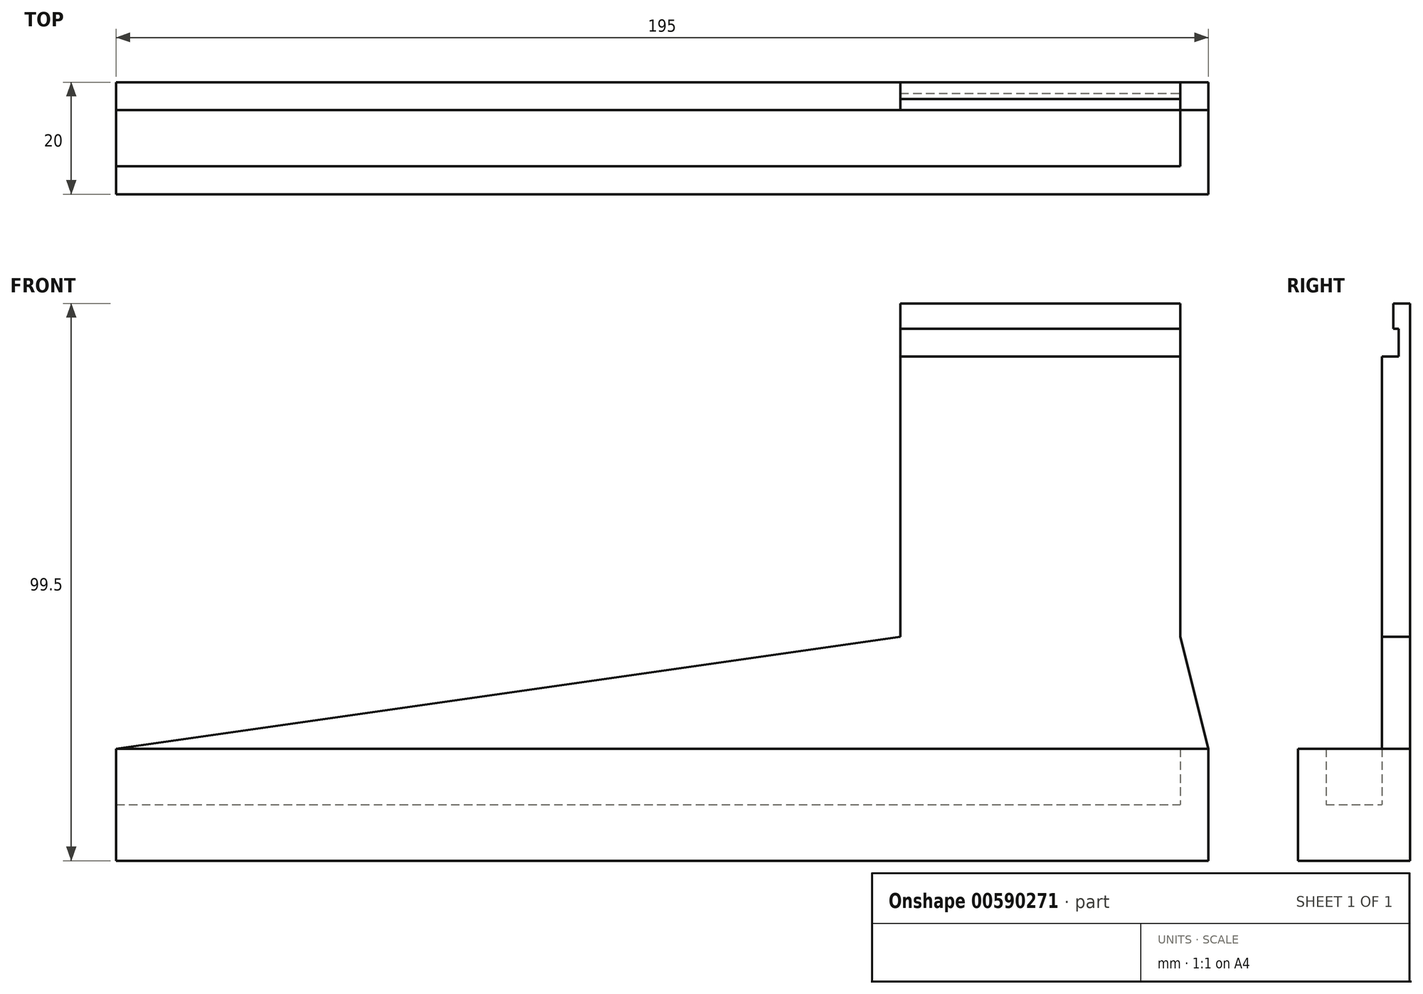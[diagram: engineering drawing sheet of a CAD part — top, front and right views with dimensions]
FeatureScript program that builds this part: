
annotation { "Feature Type Name" : "Feature", "Feature Type Description" : "" }
export const myFeature = defineFeature(function(context is Context, id is Id, definition is map)
    precondition{}
    {
        {
            var Q0;
            Q0=qCreatedBy(makeId("Top.planeOp"),FACE);
            var sketch = newSketch(context, id + "F0", { "sketchPlane" : qUnion([Q0])});
            skLineSegment(sketch, "E0.bottom", {"start": v(0, 0) * mm, "end": v(190, 0) * mm});
            skLineSegment(sketch, "E0.top", {"start": v(0, 5) * mm, "end": v(190, 5) * mm});
            skLineSegment(sketch, "E0.left", {"start": v(0, 0) * mm, "end": v(0, 5) * mm});
            skLineSegment(sketch, "E0.right", {"start": v(190, 0) * mm, "end": v(190, 5) * mm});
            skLineSegment(sketch, "E1.bottom", {"start": v(190, 0) * mm, "end": v(195, 0) * mm});
            skLineSegment(sketch, "E1.top", {"start": v(190, 20) * mm, "end": v(195, 20) * mm});
            skLineSegment(sketch, "E1.left", {"start": v(190, 0) * mm, "end": v(190, 20) * mm});
            skLineSegment(sketch, "E1.right", {"start": v(195, 0) * mm, "end": v(195, 20) * mm});
            skLineSegment(sketch, "E2.bottom", {"start": v(190, 20) * mm, "end": v(0, 20) * mm});
            skLineSegment(sketch, "E2.top", {"start": v(190, 15) * mm, "end": v(0, 15) * mm});
            skLineSegment(sketch, "E2.left", {"start": v(190, 20) * mm, "end": v(190, 15) * mm});
            skLineSegment(sketch, "E2.right", {"start": v(0, 20) * mm, "end": v(0, 15) * mm});
            skSolve(sketch);
        }
        {
            var Q0;
            Q0 = qSketchRegion(id + "F0", true);
            extrude(context, id + "F1", {"entities" : qUnion([Q0]), "depth" : 20 * mm, "offsetDistance" : 25 * mm});
        }
        {
            var Q0;
            Q0=qCreatedBy(makeId("Top.planeOp"),FACE);
            var sketch = newSketch(context, id + "F2", { "sketchPlane" : qUnion([Q0])});
            skLineSegment(sketch, "E3.bottom", {"start": v(0, 5) * mm, "end": v(190, 5) * mm});
            skLineSegment(sketch, "E3.top", {"start": v(0, 15) * mm, "end": v(190, 15) * mm});
            skLineSegment(sketch, "E3.left", {"start": v(0, 5) * mm, "end": v(0, 15) * mm});
            skLineSegment(sketch, "E3.right", {"start": v(190, 5) * mm, "end": v(190, 15) * mm});
            skSolve(sketch);
        }
        {
            var Q0;
            Q0 = qSketchRegion(id + "F2", true);
            extrude(context, id + "F3", {"entities" : qUnion([Q0]), "operationType" : NewBodyOperationType.ADD, "depth" : 10 * mm, "offsetDistance" : 25 * mm});
        }
        {
            var Q0;
            Q0=makeQuery(id+"F1.opExtrude","CAP_FACE",FACE,{"disambiguationData":[OSD([sQuery(id+"F0.wireOp",EDGE,"E0.bottom"),sQuery(id+"F0.wireOp",EDGE,"E0.top"),sQuery(id+"F0.wireOp",EDGE,"E0.left"),sQuery(id+"F0.wireOp",EDGE,"E1.bottom"),sQuery(id+"F0.wireOp",EDGE,"E1.top"),sQuery(id+"F0.wireOp",EDGE,"E1.left"),sQuery(id+"F0.wireOp",EDGE,"E1.right"),sQuery(id+"F0.wireOp",EDGE,"E2.bottom"),sQuery(id+"F0.wireOp",EDGE,"E2.top"),sQuery(id+"F0.wireOp",EDGE,"E2.right")])],"isStart":false});
            var sketch = newSketch(context, id + "F4", { "sketchPlane" : qUnion([Q0])});
            skLineSegment(sketch, "E4.bottom", {"start": v(190, 15) * mm, "end": v(140, 15) * mm});
            skLineSegment(sketch, "E4.top", {"start": v(190, 20) * mm, "end": v(140, 20) * mm});
            skLineSegment(sketch, "E4.left", {"start": v(190, 15) * mm, "end": v(190, 20) * mm});
            skLineSegment(sketch, "E4.right", {"start": v(140, 15) * mm, "end": v(140, 20) * mm});
            skSolve(sketch);
        }
        {
            var Q0;
            Q0 = qSketchRegion(id + "F4", true);
            extrude(context, id + "F5", {"entities" : qUnion([Q0]), "operationType" : NewBodyOperationType.ADD, "depth" : 70 * mm, "offsetDistance" : 25 * mm});
        }
        {
            var Q0;
            Q0=makeQuery(id+"F5.boolean.opBoolean","MERGE",FACE,{"derivedFrom":[makeQuery(id+"F1.opExtrude","SWEPT_FACE",FACE,{"disambiguationData":[OSD([sQuery(id+"F0.wireOp",EDGE,"E1.top"),sQuery(id+"F0.wireOp",EDGE,"E2.bottom")])]}),makeQuery(id+"F5.opExtrude","SWEPT_FACE",FACE,{"disambiguationData":[OSD([sQuery(id+"F4.wireOp",EDGE,"E4.top")])]})]});
            var sketch = newSketch(context, id + "F6", { "sketchPlane" : qUnion([Q0])});
            skLineSegment(sketch, "E5", {"start": v(-195, 20) * mm, "end": v(-190, 20) * mm});
            skLineSegment(sketch, "E6", {"start": v(-190, 20) * mm, "end": v(-190, 40) * mm});
            skLineSegment(sketch, "E7", {"start": v(-190, 40) * mm, "end": v(-195, 20) * mm});
            skLineSegment(sketch, "E8", {"start": v(-140, 20) * mm, "end": v(-140, 40) * mm});
            skLineSegment(sketch, "E9", {"start": v(-140, 40) * mm, "end": v(0, 20) * mm});
            skLineSegment(sketch, "E10", {"start": v(0, 20) * mm, "end": v(-140, 20) * mm});
            skSolve(sketch);
        }
        {
            var Q0;
            Q0 = qSketchRegion(id + "F6", true);
            extrude(context, id + "F7", {"entities" : qUnion([Q0]), "operationType" : NewBodyOperationType.ADD, "oppositeDirection" : true, "depth" : 5 * mm, "offsetDistance" : 25 * mm});
        }
        {
            var Q0;
            Q0=makeQuery(id+"F5.opExtrude","CAP_FACE",FACE,{"disambiguationData":[OSD([sQuery(id+"F4.wireOp",EDGE,"E4.bottom"),sQuery(id+"F4.wireOp",EDGE,"E4.top"),sQuery(id+"F4.wireOp",EDGE,"E4.left"),sQuery(id+"F4.wireOp",EDGE,"E4.right")])],"isStart":false});
            var sketch = newSketch(context, id + "F8", { "sketchPlane" : qUnion([Q0])});
            skLineSegment(sketch, "E11.bottom", {"start": v(140, 20) * mm, "end": v(190, 20) * mm});
            skLineSegment(sketch, "E11.top", {"start": v(140, 18) * mm, "end": v(190, 18) * mm});
            skLineSegment(sketch, "E11.left", {"start": v(140, 20) * mm, "end": v(140, 18) * mm});
            skLineSegment(sketch, "E11.right", {"start": v(190, 20) * mm, "end": v(190, 18) * mm});
            skSolve(sketch);
        }
        {
            var Q0;
            Q0 = qSketchRegion(id + "F8", true);
            extrude(context, id + "F9", {"entities" : qUnion([Q0]), "operationType" : NewBodyOperationType.ADD, "depth" : 5 * mm, "offsetDistance" : 25 * mm});
        }
        {
            var Q0;
            Q0=makeQuery(id+"F9.opExtrude","CAP_FACE",FACE,{"disambiguationData":[OSD([sQuery(id+"F8.wireOp",EDGE,"E11.bottom"),sQuery(id+"F8.wireOp",EDGE,"E11.top"),sQuery(id+"F8.wireOp",EDGE,"E11.left"),sQuery(id+"F8.wireOp",EDGE,"E11.right")])],"isStart":false});
            var sketch = newSketch(context, id + "F10", { "sketchPlane" : qUnion([Q0])});
            skLineSegment(sketch, "E12.bottom", {"start": v(140, 20) * mm, "end": v(190, 20) * mm});
            skLineSegment(sketch, "E12.top", {"start": v(140, 17) * mm, "end": v(190, 17) * mm});
            skLineSegment(sketch, "E12.left", {"start": v(140, 20) * mm, "end": v(140, 17) * mm});
            skLineSegment(sketch, "E12.right", {"start": v(190, 20) * mm, "end": v(190, 17) * mm});
            skSolve(sketch);
        }
        {
            var Q0;
            Q0 = qSketchRegion(id + "F10", true);
            extrude(context, id + "F11", {"entities" : qUnion([Q0]), "operationType" : NewBodyOperationType.ADD, "depth" : 4.5 * mm, "offsetDistance" : 25 * mm});
        }
    });
